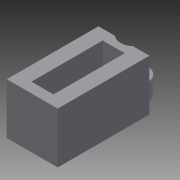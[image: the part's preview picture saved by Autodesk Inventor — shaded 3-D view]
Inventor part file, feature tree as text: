
AUTODESK INVENTOR PART (.ipt)
format: ipt  version: 2013 (Build 170138000, 138)  size: 112,640 bytes
history: native  units: mm
features: extrude x3, sketch x3, fillet x1, projected_geometry x1
ambient origin geometry x8: Origin, YZ Plane, XZ Plane, XY Plane, X Axis, Y Axis, Z Axis, Center Point
bodies: Solid1 (feature_tree)
feature tree (8):
  extrude  "Extrusion1"  Depth=27.0mm
  extrude  "Extrusion2"  Depth=8.0mm
  fillet  "Fillet2"  Radius=3.0mm
  extrude  "Extrusion3"  Depth=6.5mm
  sketch  "Sketch1"  dims[d2=15.0mm d3=27.0mm]
  sketch  "Sketch2"  dims[d5=15.0mm d6=0.0mm d7=8.0mm d8=3.0mm]
  sketch  "Sketch3"  dims[d9=3.0mm d14=6.5mm d16=21.0mm d17=10.0mm d18=0.0mm d19=3.0mm d20=1.0mm d21=10.0mm d22=0.0mm]
  projected_geometry  "Projected Loop1"
